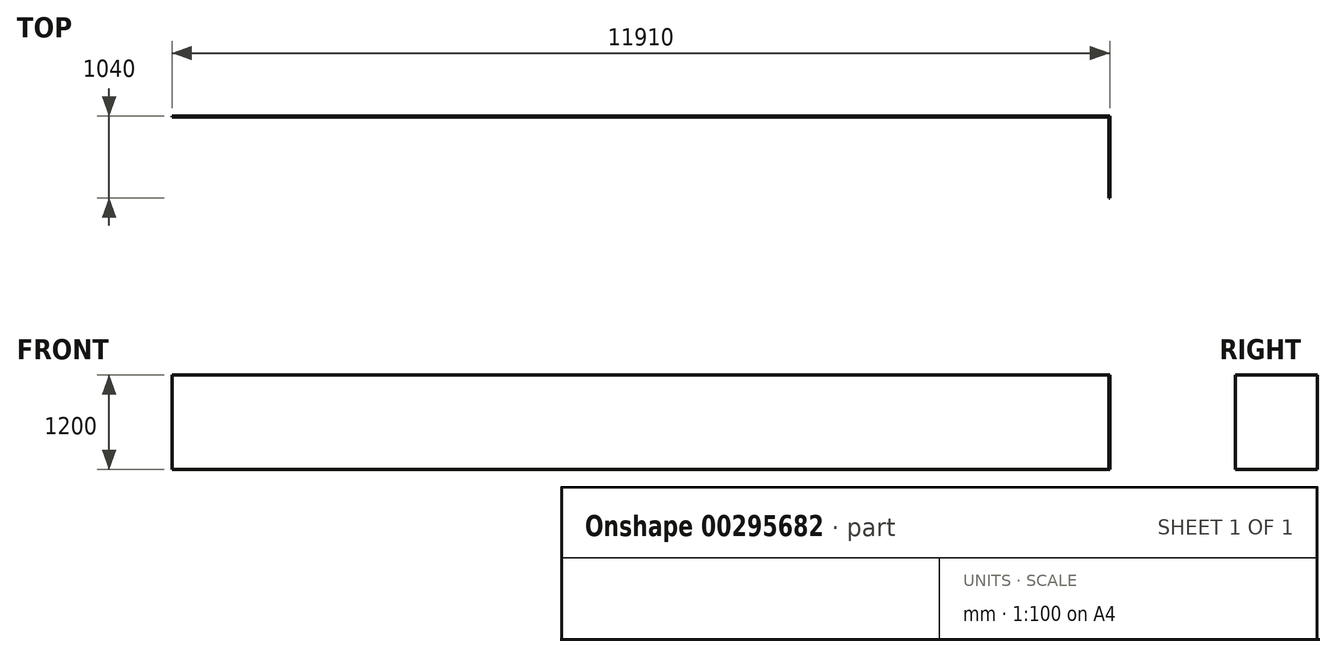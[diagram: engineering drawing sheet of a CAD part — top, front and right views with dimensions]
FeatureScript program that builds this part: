
annotation { "Feature Type Name" : "Feature", "Feature Type Description" : "" }
export const myFeature = defineFeature(function(context is Context, id is Id, definition is map)
    precondition{}
    {
        {
            var Q0;
            Q0=qCreatedBy(makeId("Top.planeOp"),FACE);
            var sketch = newSketch(context, id + "F0", { "sketchPlane" : qUnion([Q0])});
            skLineSegment(sketch, "E0", {"start": v(0, 0) * mm, "end": v(0, 1030) * mm});
            skLineSegment(sketch, "E1", {"start": v(0, 1030) * mm, "end": v(-11900, 1030) * mm});
            skLineSegment(sketch, "E2", {"start": v(-11900, 1030) * mm, "end": v(-11900, 1040) * mm});
            skLineSegment(sketch, "E3", {"start": v(-11900, 1040) * mm, "end": v(10, 1040) * mm});
            skLineSegment(sketch, "E4", {"start": v(10, 1040) * mm, "end": v(10, 0) * mm});
            skLineSegment(sketch, "E5", {"start": v(10, 0) * mm, "end": v(0, 0) * mm});
            skSolve(sketch);
        }
        {
            var Q0;
            Q0 = qSketchRegion(id + "F0", true);
            extrude(context, id + "F1", {"entities" : qUnion([Q0]), "depth" : 1200 * mm});
        }
    });
